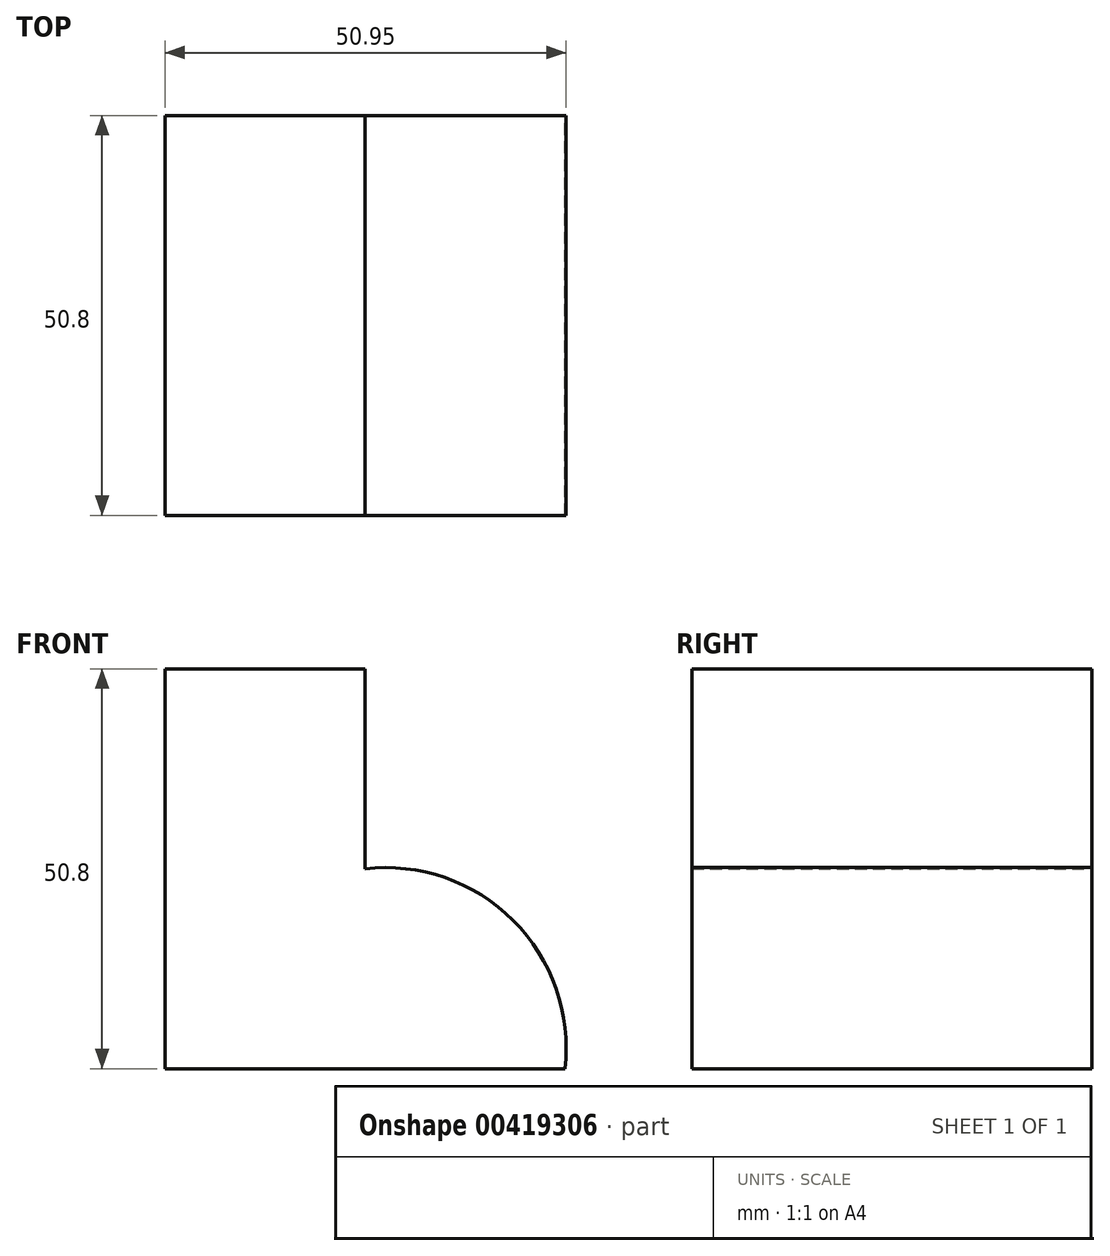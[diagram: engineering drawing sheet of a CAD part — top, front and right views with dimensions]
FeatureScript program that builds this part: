
annotation { "Feature Type Name" : "Feature", "Feature Type Description" : "" }
export const myFeature = defineFeature(function(context is Context, id is Id, definition is map)
    precondition{}
    {
        {
            var Q0;
            Q0=qCreatedBy(makeId("Front.planeOp"),FACE);
            var sketch = newSketch(context, id + "F0", { "sketchPlane" : qUnion([Q0])});
            skLineSegment(sketch, "E0", {"start": v(0, 0) * mm, "end": v(-50.8, 0) * mm});
            skLineSegment(sketch, "E1", {"start": v(-50.8, 0) * mm, "end": v(-50.8, 50.8) * mm});
            skLineSegment(sketch, "E2", {"start": v(-50.8, 50.8) * mm, "end": v(-25.4, 50.8) * mm});
            skLineSegment(sketch, "E3", {"start": v(-25.4, 50.8) * mm, "end": v(-25.4, 25.4) * mm});
            skArc(sketch, "E4", {"start": v(0, 0) * mm, "mid": v(-6.57, 18.83) * mm, "end": v(-25.4, 25.4) * mm});
            skSolve(sketch);
        }
        {
            var Q0;
            Q0=makeQuery(id+"F0.imprint","IMPRINT",FACE,{"disambiguationData":[TD([[makeQuery(id+"F0.imprint","IMPRINT",EDGE,{"derivedFrom":sQuery(id+"F0.wireOp",EDGE,"E0")}),-1.0]])]});
            extrude(context, id + "F1", {"entities" : qUnion([Q0]), "depth" : 50.8 * mm});
        }
    });
